# Revit family: Módulo de Comando Endereçável Sirius MSC2-D ILUMAC
name_source: partatom
category: Dispositivos de alarme de incêndio
units: mm (PartAtom-declared; Revit-internal decimal feet)

## family parameters
Com base no plano de trabalho = Não
Compartilhado = Não
Corte com vazios quando carregada = Não
Cota do conector redondo = Utilizar diâmetro
Manter orientação da anotação = Não
Número OmniClass = 23.80.30.11.17
Ponto de cálculo do ambiente = Não
Sempre na vertical = Sim
Tipo de parte = Normal
Título OmniClass = Distribution Boards and Control Panels

## types (2) — shared parameters
Dimensões (AxLxP) = 90x90x55mm
Endereços programáveis = 001 à 125 (por laço)
Endereços utilizados = 1 endereço
Fixação = Sobrepor c/ entrada superior/inferior p/ tubo 3/4"
Grau de proteção = IP42 (à prova de respingo d’água)
Material da caixa = Caixa plástica ABS na cor branco
Protocolo de comunicação = ALF-1000-2 (proprietário)
Quant. de dispositivos na entrada = Até 20 dispositivos convencionais ILUMAC
limitado à corrente de 2mA total em supervisão**
Secção máxima do cabo = 2,5mm²
Tensão nominal = 24Vcc
Tipo de entrada = 1 laço (zona) supervisionado em Classe B
Umidade relativa = 0 à 95% (sem condensação)
zero-valued in all types: Elevação padrão

## per-type parameters (varying)
| type | Acionamento | Consumo da fonte auxiliar ou V+ | Consumo do laço endereçável | Código do Produto | Descrição | Fabricante | Limitação Saída de Contato Seco | Limitação Saída para Sirene | Modelo | Normas técnicas aplicáveis | Peso | Resistor de final de linha (RFL) | Temperatura de operação | Tensão de operação | Tipos de saída |
| MZE2-D |  | 4,5mA em alarme sem dispositivo* | 800uA em supervisão / 400uA em alarme | 004051 |  |  |  |  |  | NBR 17240 / ISO 7240-18 / BS 5839 | 130g | 10KΩ | -5 à 55oC | 19 a 31Vcc |  |
| MSC2-D | Em pré-alarme (não respeita retardo do sistema)
Em alarme (respeita retardo do sistema)
Possui trimpot para retardo externo ao sistema | 60mA em alarme sem dispositivo* | 1.5mA em supervisão / 2mA em alarme | 004053 | Módulo de Comando Endereçável Sirius MSC2-D | ILUMAC | Tensão máx 30V / 1A (carga resistiva) | 900mA @ 28Vcc | MSC2-D | NBR 17240 / ISO 7240-18 | 145g | 10KΩ - monitora a saída para sirenes | 0 à 50oC | 20 a 30Vcc | 1 saída contato seco SPDT-NA
1 saída para sirenes convencionais |
